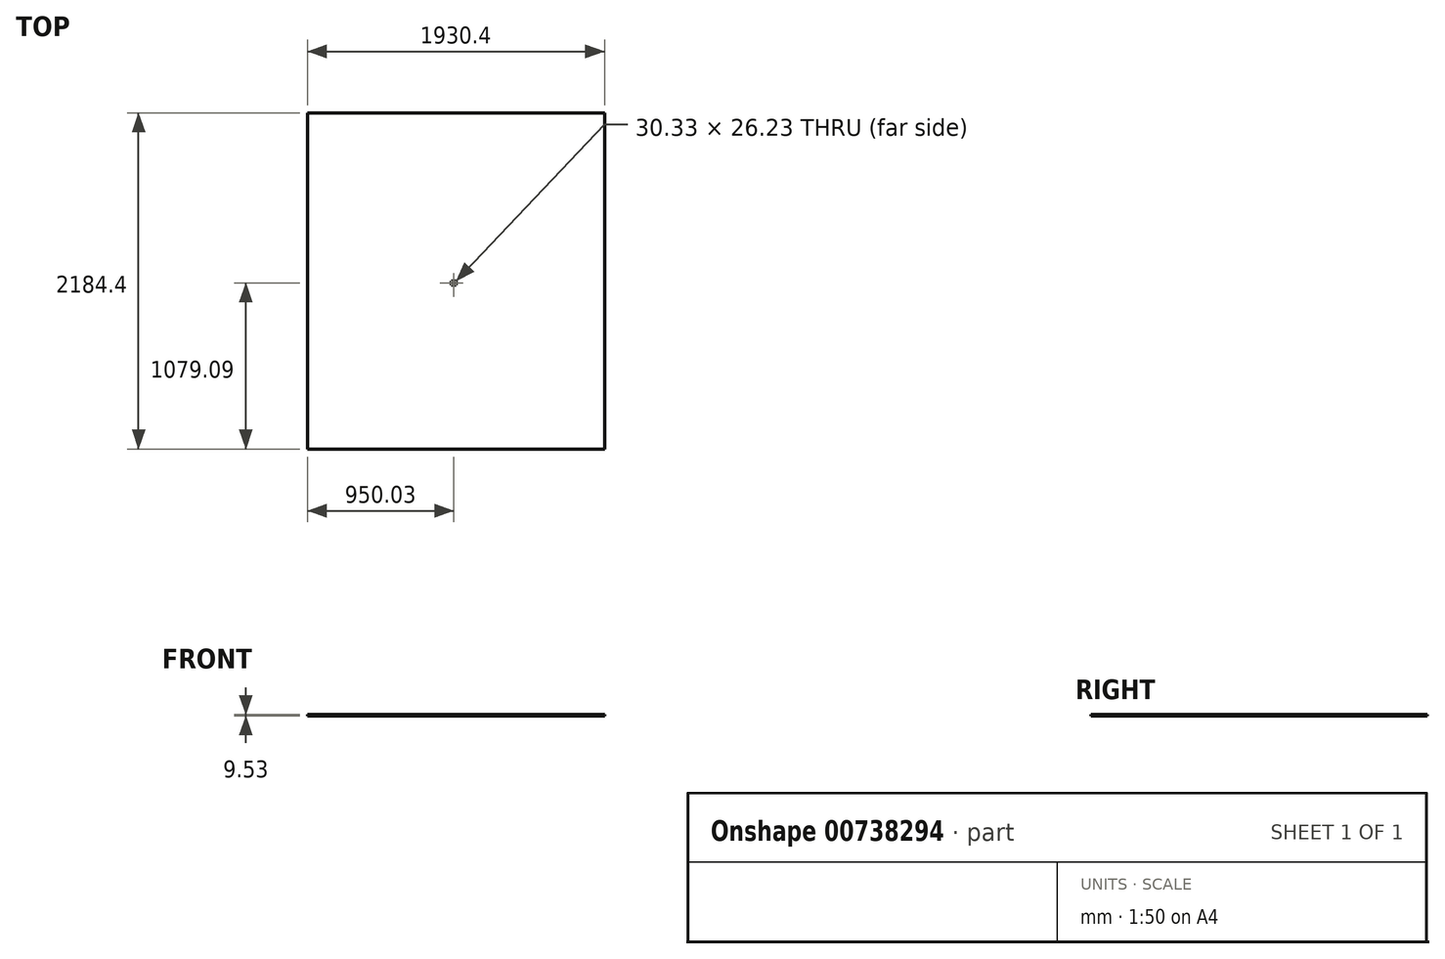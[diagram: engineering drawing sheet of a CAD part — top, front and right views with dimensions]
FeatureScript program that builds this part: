
annotation { "Feature Type Name" : "Feature", "Feature Type Description" : "" }
export const myFeature = defineFeature(function(context is Context, id is Id, definition is map)
    precondition{}
    {
        {
            var Q0;
            Q0=qCreatedBy(makeId("Top.planeOp"),FACE);
            var sketch = newSketch(context, id + "F0", { "sketchPlane" : qUnion([Q0])});
            skLineSegment(sketch, "E0.bottom", {"start": v(15.17, 13.11) * mm, "end": v(-15.17, 13.11) * mm});
            skLineSegment(sketch, "E0.top", {"start": v(15.17, -13.11) * mm, "end": v(-15.17, -13.11) * mm});
            skLineSegment(sketch, "E0.left", {"start": v(15.17, 13.11) * mm, "end": v(15.17, -13.11) * mm});
            skLineSegment(sketch, "E0.right", {"start": v(-15.17, 13.11) * mm, "end": v(-15.17, -13.11) * mm});
            skPoint(sketch, "E0.middle", {"position": v(0, 0) * mm});
            skLineSegment(sketch, "E1.bottom", {"start": v(980.37, 1105.31) * mm, "end": v(-950.03, 1105.31) * mm});
            skLineSegment(sketch, "E1.top", {"start": v(980.37, -1079.09) * mm, "end": v(-950.03, -1079.09) * mm});
            skLineSegment(sketch, "E1.left", {"start": v(980.37, 1105.31) * mm, "end": v(980.37, -1079.09) * mm});
            skLineSegment(sketch, "E1.right", {"start": v(-950.03, 1105.31) * mm, "end": v(-950.03, -1079.09) * mm});
            skPoint(sketch, "E1.middle", {"position": v(15.17, 13.11) * mm});
            skSolve(sketch);
        }
        {
            var Q0;
            Q0=makeQuery(id+"F0.imprint","IMPRINT",FACE,{"disambiguationData":[TD([[makeQuery(id+"F0.imprint","IMPRINT",EDGE,{"derivedFrom":sQuery(id+"F0.wireOp",EDGE,"E0.bottom")}),-1.0]])]});
            extrude(context, id + "F1", {"entities" : qUnion([Q0]), "depth" : 9.52 * mm, "offsetDistance" : 25.4 * mm});
        }
    });
